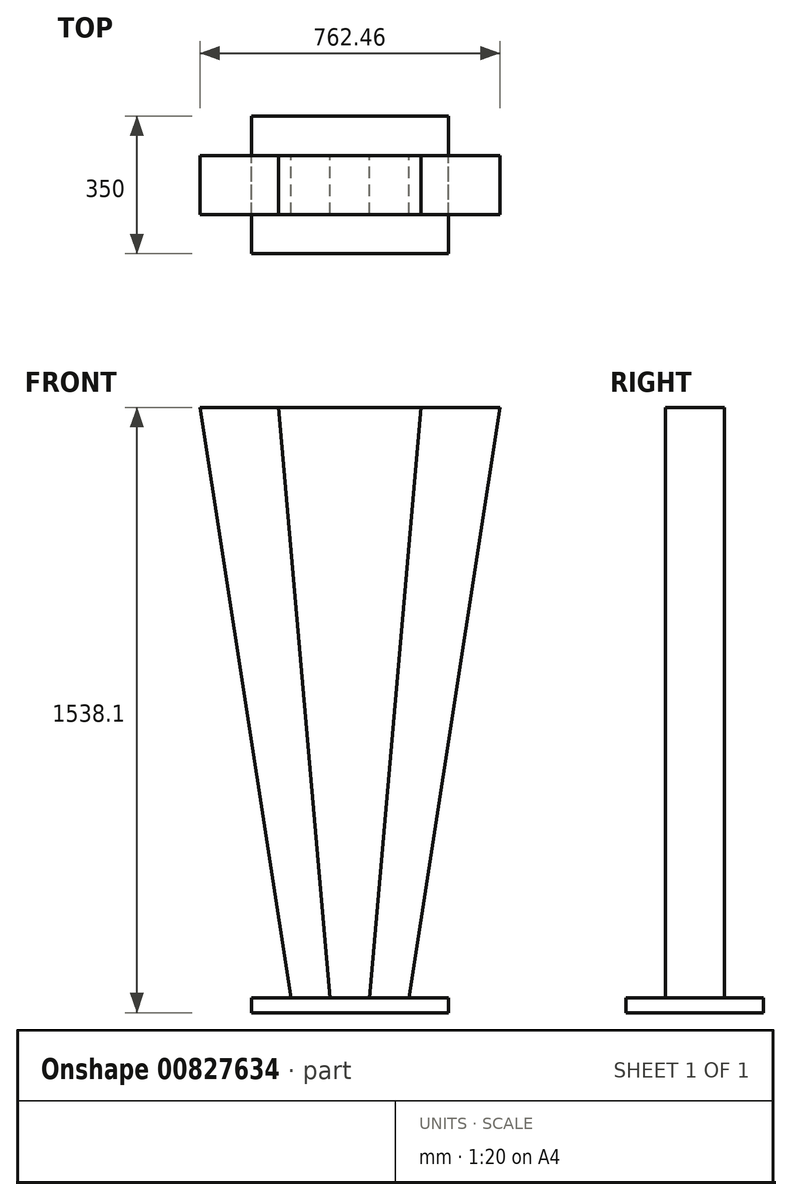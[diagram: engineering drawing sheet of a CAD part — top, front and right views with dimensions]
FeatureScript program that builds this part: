
annotation { "Feature Type Name" : "Feature", "Feature Type Description" : "" }
export const myFeature = defineFeature(function(context is Context, id is Id, definition is map)
    precondition{}
    {
        {
            var Q0;
            Q0=qCreatedBy(makeId("Front.planeOp"),FACE);
            var sketch = newSketch(context, id + "F0", { "sketchPlane" : qUnion([Q0])});
            skLineSegment(sketch, "E0", {"start": v(-50, 0) * mm, "end": v(-181.23, 1500) * mm});
            skLineSegment(sketch, "E1", {"start": v(0, 0) * mm, "end": v(0, 1500) * mm, "construction": true});
            skLineSegment(sketch, "E2", {"start": v(-181.23, 1500) * mm, "end": v(-381.23, 1500) * mm});
            skLineSegment(sketch, "E3", {"start": v(-381.23, 1500) * mm, "end": v(-150, 0) * mm});
            skLineSegment(sketch, "E4", {"start": v(-150, 0) * mm, "end": v(-50, 0) * mm});
            skLineSegment(sketch, "E5.MirrorCS", {"start": v(181.23, 1500) * mm, "end": v(381.23, 1500) * mm});
            skLineSegment(sketch, "E6.MirrorCS", {"start": v(50, 0) * mm, "end": v(181.23, 1500) * mm});
            skLineSegment(sketch, "E7.MirrorCS", {"start": v(381.23, 1500) * mm, "end": v(150, 0) * mm});
            skLineSegment(sketch, "E8.MirrorCS", {"start": v(150, 0) * mm, "end": v(50, 0) * mm});
            skLineSegment(sketch, "E9", {"start": v(-181.23, 1500) * mm, "end": v(181.23, 1500) * mm});
            skLineSegment(sketch, "E10", {"start": v(50, 0) * mm, "end": v(-50, 0) * mm});
            skSolve(sketch);
        }
        {
            var Q0;
            Q0=makeQuery(id+"F0.imprint","IMPRINT",FACE,{"disambiguationData":[TD([[makeQuery(id+"F0.imprint","IMPRINT",EDGE,{"derivedFrom":sQuery(id+"F0.wireOp",EDGE,"E0")}),1.0]])]});
            var Q1;
            Q1=makeQuery(id+"F0.imprint","IMPRINT",FACE,{"disambiguationData":[TD([[makeQuery(id+"F0.imprint","IMPRINT",EDGE,{"derivedFrom":sQuery(id+"F0.wireOp",EDGE,"E5.MirrorCS")}),-1.0]])]});
            extrude(context, id + "F1", {"entities" : qUnion([Q0, Q1]), "endBound" : BoundingType.SYMMETRIC, "depth" : 150 * mm, "offsetDistance" : 25 * mm});
        }
        {
            var Q0;
            Q0=makeQuery(id+"F0.imprint","IMPRINT",FACE,{"disambiguationData":[TD([[makeQuery(id+"F0.imprint","IMPRINT",EDGE,{"derivedFrom":sQuery(id+"F0.wireOp",EDGE,"E0")}),-1.0]])]});
            extrude(context, id + "F2", {"entities" : qUnion([Q0]), "endBound" : BoundingType.SYMMETRIC, "depth" : 150 * mm, "offsetDistance" : 25 * mm});
        }
        {
            var Q0;
            Q0=qCreatedBy(makeId("Top.planeOp"),FACE);
            var sketch = newSketch(context, id + "F3", { "sketchPlane" : qUnion([Q0])});
            skLineSegment(sketch, "E11.bottom", {"start": v(250, -175) * mm, "end": v(-250, -175) * mm});
            skLineSegment(sketch, "E11.top", {"start": v(250, 175) * mm, "end": v(-250, 175) * mm});
            skLineSegment(sketch, "E11.left", {"start": v(250, -175) * mm, "end": v(250, 175) * mm});
            skLineSegment(sketch, "E11.right", {"start": v(-250, -175) * mm, "end": v(-250, 175) * mm});
            skPoint(sketch, "E11.middle", {"position": v(0, 0) * mm});
            skSolve(sketch);
        }
        {
            var Q0;
            Q0 = qSketchRegion(id + "F3", true);
            extrude(context, id + "F4", {"entities" : qUnion([Q0]), "oppositeDirection" : true, "depth" : 38.1 * mm, "offsetDistance" : 25 * mm});
        }
    });
